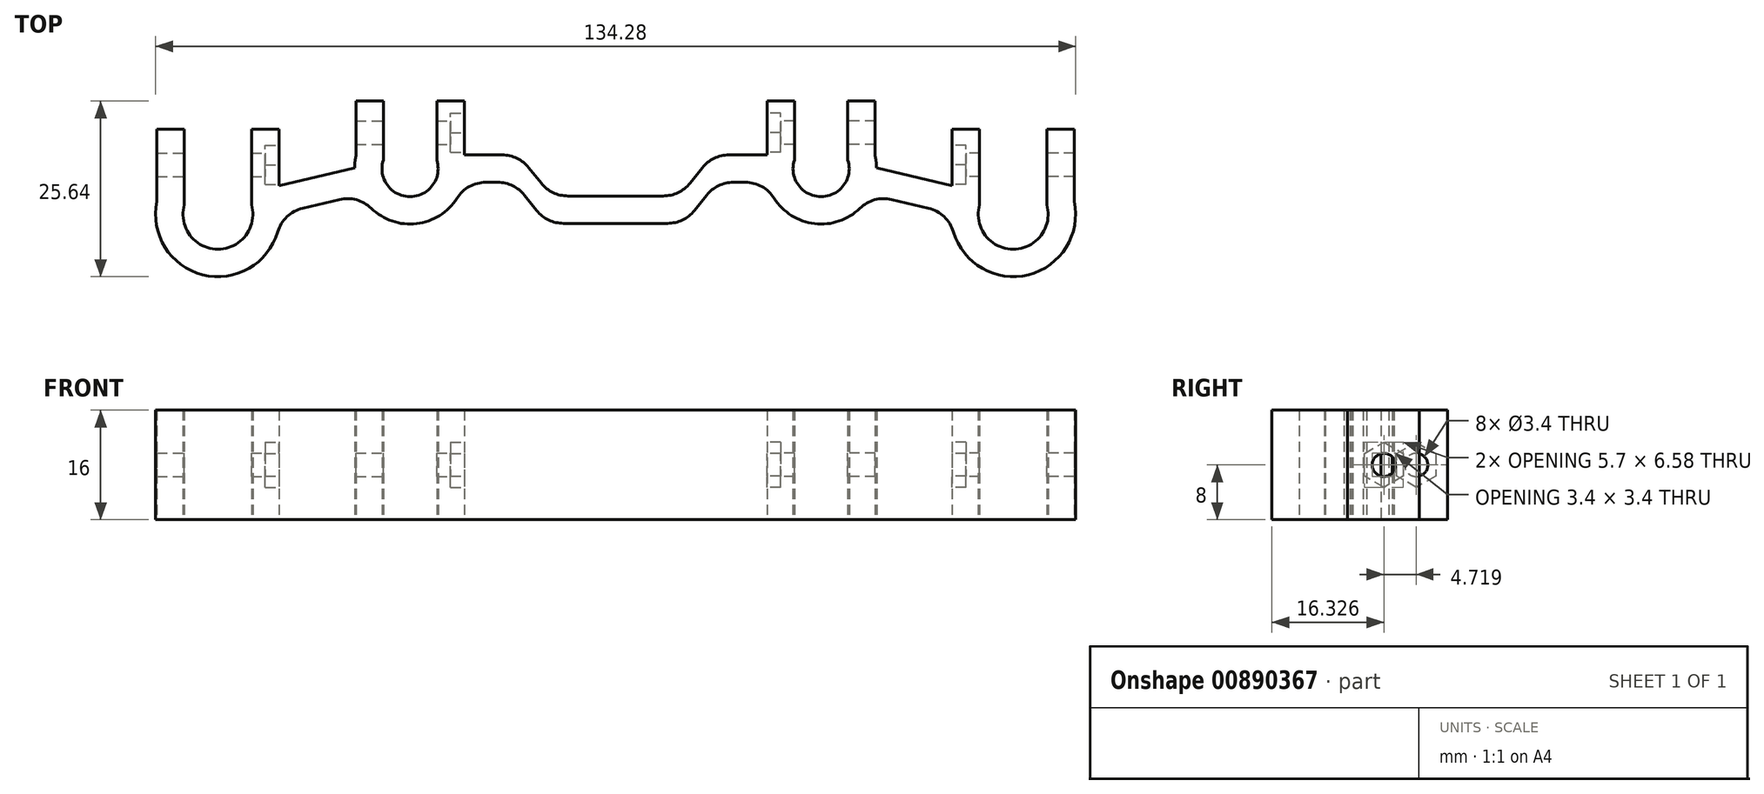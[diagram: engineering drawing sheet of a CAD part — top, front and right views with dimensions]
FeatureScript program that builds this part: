
annotation { "Feature Type Name" : "Feature", "Feature Type Description" : "" }
export const myFeature = defineFeature(function(context is Context, id is Id, definition is map)
    precondition{}
    {
        {
            var Q0;
            Q0=qCreatedBy(makeId("Top.planeOp"),FACE);
            var sketch = newSketch(context, id + "F0", { "sketchPlane" : qUnion([Q0])});
            skArc(sketch, "E0", {"start": v(-33.9, 1.26) * mm, "mid": v(-30, -4.1) * mm, "end": v(-26.1, 1.26) * mm});
            skArc(sketch, "E1", {"start": v(-62.94, -5.27) * mm, "mid": v(-58.04, -11.78) * mm, "end": v(-53.14, -5.27) * mm});
            skArc(sketch, "E2", {"start": v(-62.94, 0.99) * mm, "mid": v(-58.04, -15.78) * mm, "end": v(-53.14, 0.99) * mm});
            skArc(sketch, "E3", {"start": v(-33.9, 7.1) * mm, "mid": v(-30, -8.1) * mm, "end": v(-26.1, 7.1) * mm});
            skLineSegment(sketch, "E4", {"start": v(-58.04, -6.68) * mm, "end": v(-30, 0) * mm, "construction": true});
            skLineSegment(sketch, "E5", {"start": v(0, 0) * mm, "end": v(-30, 0) * mm, "construction": true});
            skLineSegment(sketch, "E6", {"start": v(-48.94, -6.57) * mm, "end": v(-37.17, -3.76) * mm});
            skLineSegment(sketch, "E7", {"start": v(-49.87, -2.68) * mm, "end": v(-38.1, 0.13) * mm});
            skLineSegment(sketch, "E8", {"start": v(-22.15, -2) * mm, "end": v(-16.15, -2) * mm});
            skLineSegment(sketch, "E9", {"start": v(-14.15, 2) * mm, "end": v(-22.15, 2) * mm});
            skLineSegment(sketch, "E10", {"start": v(-66.94, -4.78) * mm, "end": v(-66.94, 5.73) * mm});
            skLineSegment(sketch, "E11", {"start": v(-66.94, 5.73) * mm, "end": v(-62.94, 5.73) * mm});
            skLineSegment(sketch, "E12", {"start": v(-62.94, 5.73) * mm, "end": v(-62.94, -5.27) * mm});
            skLineSegment(sketch, "E13", {"start": v(-58.04, -5.27) * mm, "end": v(-66.94, -5.27) * mm, "construction": true});
            skLineSegment(sketch, "E14", {"start": v(-58.04, -6.68) * mm, "end": v(-58.04, 14.87) * mm, "construction": true});
            skLineSegment(sketch, "E15.MirrorCS", {"start": v(-53.14, 5.73) * mm, "end": v(-53.14, -5.27) * mm});
            skLineSegment(sketch, "E16.MirrorCS", {"start": v(-49.14, 5.73) * mm, "end": v(-53.14, 5.73) * mm});
            skLineSegment(sketch, "E17.MirrorCS", {"start": v(-49.14, -4.78) * mm, "end": v(-49.14, 5.73) * mm});
            skLineSegment(sketch, "E18", {"start": v(-30, 0) * mm, "end": v(-30, 14.05) * mm, "construction": true});
            skLineSegment(sketch, "E19", {"start": v(-37.9, 9.86) * mm, "end": v(-33.9, 9.86) * mm});
            skLineSegment(sketch, "E20", {"start": v(-33.9, 9.86) * mm, "end": v(-33.9, 1.26) * mm});
            skLineSegment(sketch, "E21.MirrorCS", {"start": v(-26.1, 9.86) * mm, "end": v(-26.1, 1.26) * mm});
            skLineSegment(sketch, "E22.MirrorCS", {"start": v(-22.1, 9.86) * mm, "end": v(-26.1, 9.86) * mm});
            skLineSegment(sketch, "E23", {"start": v(-37.9, 9.86) * mm, "end": v(-37.9, 1.79) * mm});
            skLineSegment(sketch, "E24.MirrorCS", {"start": v(-22.1, 9.86) * mm, "end": v(-22.1, 2) * mm});
            skPoint(sketch, "E25.orphan", {"position": v(-22.1, 1.79) * mm});
            skLineSegment(sketch, "E26", {"start": v(-14.15, 2) * mm, "end": v(-9.36, -4) * mm});
            skLineSegment(sketch, "E27", {"start": v(-9.36, -4) * mm, "end": v(-6, -4) * mm});
            skLineSegment(sketch, "E28", {"start": v(-14.8, -2) * mm, "end": v(-10, -8) * mm});
            skLineSegment(sketch, "E29", {"start": v(-10, -8) * mm, "end": v(0, -8) * mm});
            skLineSegment(sketch, "E30", {"start": v(0, -8) * mm, "end": v(0, -4) * mm});
            skLineSegment(sketch, "E31", {"start": v(-6, -4) * mm, "end": v(0, -4) * mm});
            skLineSegment(sketch, "E32", {"start": v(-16.15, -2) * mm, "end": v(-14.8, -2) * mm});
            skLineSegment(sketch, "E33", {"start": v(-9.36, -4) * mm, "end": v(-9.36, 12.5) * mm, "construction": true});
            skSolve(sketch);
        }
        {
            var Q0;
            Q0 = qSketchRegion(id + "F0", true);
            extrude(context, id + "F1", {"entities" : qUnion([Q0]), "depth" : 16 * mm, "offsetDistance" : 25 * mm});
        }
        {
            var Q0;
            Q0=makeQuery(id+"F1.opExtrude","SWEPT_FACE",FACE,{"disambiguationData":[OSD([sQuery(id+"F0.wireOp",EDGE,"E24.MirrorCS")])]});
            var sketch = newSketch(context, id + "F2", { "sketchPlane" : qUnion([Q0])});
            skCircle(sketch, "E34.cCircle", {"center": v(5.26, 8) * mm, "radius": 2.85 * mm, "construction": true});
            skLineSegment(sketch, "E34.0", {"start": v(8.11, 9.65) * mm, "end": v(8.11, 6.35) * mm});
            skLineSegment(sketch, "E34.1", {"start": v(8.11, 6.35) * mm, "end": v(5.26, 4.7) * mm});
            skLineSegment(sketch, "E34.2", {"start": v(5.26, 4.7) * mm, "end": v(2.41, 6.35) * mm});
            skLineSegment(sketch, "E34.3", {"start": v(2.41, 6.35) * mm, "end": v(2.41, 9.65) * mm});
            skLineSegment(sketch, "E34.4", {"start": v(2.41, 9.65) * mm, "end": v(5.26, 11.3) * mm});
            skLineSegment(sketch, "E34.5", {"start": v(5.26, 11.3) * mm, "end": v(8.11, 9.65) * mm});
            skPoint(sketch, "E34.0.midPoint", {"position": v(8.11, 8) * mm});
            skLineSegment(sketch, "E35", {"start": v(9.86, 8) * mm, "end": v(-7.7, 8) * mm, "construction": true});
            skCircle(sketch, "E36", {"center": v(5.26, 8) * mm, "radius": 1.7 * mm});
            skSolve(sketch);
        }
        {
            var Q0;
            Q0=makeQuery(id+"F2.imprint","IMPRINT",FACE,{"disambiguationData":[TD([[makeQuery(id+"F2.imprint","IMPRINT",EDGE,{"derivedFrom":sQuery(id+"F2.wireOp",EDGE,"b88b7a63-ffb0-4f3f-a911-7858551cdc820.MirrorC")}),-1.0]])]});
            var Q1;
            Q1=makeQuery(id+"F2.imprint","IMPRINT",FACE,{"disambiguationData":[TD([[makeQuery(id+"F2.imprint","IMPRINT",EDGE,{"derivedFrom":sQuery(id+"F2.wireOp",EDGE,"E36")}),1.0]])]});
            var Q2;
            Q2=makeQuery(id+"F1.opExtrude","SWEPT_FACE",FACE,{"disambiguationData":[OSD([sQuery(id+"F0.wireOp",EDGE,"E23")])]});
            extrude(context, id + "F3", {"entities" : qUnion([Q0, Q1]), "operationType" : NewBodyOperationType.REMOVE, "endBound" : BoundingType.UP_TO_SURFACE, "oppositeDirection" : true, "depth" : 25 * mm, "endBoundEntityFace" : qUnion([Q2]), "offsetDistance" : 25 * mm});
        }
        {
            var Q0;
            Q0=makeQuery(id+"F2.imprint","IMPRINT",FACE,{"disambiguationData":[TD([[makeQuery(id+"F2.imprint","IMPRINT",EDGE,{"derivedFrom":sQuery(id+"F2.wireOp",EDGE,"1b03209d-ab96-45ee-9a79-0f29908199c00.MirrorCS")}),1.0]])]});
            var Q1;
            Q1=makeQuery(id+"F2.imprint","IMPRINT",FACE,{"disambiguationData":[TD([[makeQuery(id+"F2.imprint","IMPRINT",EDGE,{"derivedFrom":sQuery(id+"F2.wireOp",EDGE,"E34.0")}),-1.0]])]});
            extrude(context, id + "F4", {"entities" : qUnion([Q0, Q1]), "operationType" : NewBodyOperationType.REMOVE, "oppositeDirection" : true, "depth" : 2 * mm, "offsetDistance" : 25 * mm});
        }
        {
            var Q0;
            Q0=makeQuery(id+"F1.opExtrude","SWEPT_FACE",FACE,{"disambiguationData":[OSD([sQuery(id+"F0.wireOp",EDGE,"E17.MirrorCS")])]});
            var sketch = newSketch(context, id + "F5", { "sketchPlane" : qUnion([Q0])});
            skCircle(sketch, "E37.cCircle", {"center": v(0.55, 8) * mm, "radius": 2.85 * mm, "construction": true});
            skLineSegment(sketch, "E37.0", {"start": v(3.4, 9.65) * mm, "end": v(3.4, 6.35) * mm});
            skLineSegment(sketch, "E37.1", {"start": v(3.4, 6.35) * mm, "end": v(0.55, 4.7) * mm});
            skLineSegment(sketch, "E37.2", {"start": v(0.55, 4.7) * mm, "end": v(-2.3, 6.35) * mm});
            skLineSegment(sketch, "E37.3", {"start": v(-2.3, 6.35) * mm, "end": v(-2.3, 9.65) * mm});
            skLineSegment(sketch, "E37.4", {"start": v(-2.3, 9.65) * mm, "end": v(0.55, 11.3) * mm});
            skLineSegment(sketch, "E37.5", {"start": v(0.55, 11.3) * mm, "end": v(3.4, 9.65) * mm});
            skPoint(sketch, "E37.0.midPoint", {"position": v(3.4, 8) * mm});
            skLineSegment(sketch, "E38", {"start": v(5.73, 8) * mm, "end": v(4.73, 8) * mm, "construction": true});
            skPoint(sketch, "E38.startSnap0", {"position": v(5.73, 8) * mm});
            skCircle(sketch, "E39", {"center": v(0.55, 8) * mm, "radius": 1.7 * mm});
            skSolve(sketch);
        }
        {
            var Q0;
            Q0=makeQuery(id+"F5.imprint","IMPRINT",FACE,{"disambiguationData":[TD([[makeQuery(id+"F5.imprint","IMPRINT",EDGE,{"derivedFrom":sQuery(id+"F5.wireOp",EDGE,"b51dffc8-de77-4591-ae2f-6b328c8c791c0.MirrorC")}),-1.0]])]});
            var Q1;
            Q1=makeQuery(id+"F5.imprint","IMPRINT",FACE,{"disambiguationData":[TD([[makeQuery(id+"F5.imprint","IMPRINT",EDGE,{"derivedFrom":sQuery(id+"F5.wireOp",EDGE,"E39")}),1.0]])]});
            var Q2;
            Q2=makeQuery(id+"F1.opExtrude","SWEPT_FACE",FACE,{"disambiguationData":[OSD([sQuery(id+"F0.wireOp",EDGE,"E10")])]});
            extrude(context, id + "F6", {"entities" : qUnion([Q0, Q1]), "operationType" : NewBodyOperationType.REMOVE, "endBound" : BoundingType.UP_TO_SURFACE, "oppositeDirection" : true, "depth" : 25 * mm, "endBoundEntityFace" : qUnion([Q2]), "offsetDistance" : 25 * mm});
        }
        {
            var Q0;
            Q0=makeQuery(id+"F5.imprint","IMPRINT",FACE,{"disambiguationData":[TD([[makeQuery(id+"F5.imprint","IMPRINT",EDGE,{"derivedFrom":sQuery(id+"F5.wireOp",EDGE,"E37.0")}),-1.0]])]});
            var Q1;
            {var subQ1=sQuery(id+"F5.wireOp",EDGE,"86751706-22c6-47e1-9a94-7943053e6f4f0.MirrorCS");Q1=makeQuery(id+"F5.imprint","IMPRINT",FACE,{"disambiguationData":[TD([[makeQuery(id+"F5.imprint","IMPRINT",EDGE,{"derivedFrom":subQ1}),1.0]])]});}
            extrude(context, id + "F7", {"entities" : qUnion([Q0, Q1]), "operationType" : NewBodyOperationType.REMOVE, "oppositeDirection" : true, "depth" : 2 * mm, "offsetDistance" : 25 * mm});
        }
        {
            var Q0;
            Q0=makeQuery(id+"F1.opExtrude","SWEPT_EDGE",EDGE,{"disambiguationData":[OSD([sQuery(id+"F0.wireOp",EDGE,"E2"),sQuery(id+"F0.wireOp",EDGE,"E6")])]});
            var Q1;
            Q1=makeQuery(id+"F1.opExtrude","SWEPT_EDGE",EDGE,{"disambiguationData":[OSD([sQuery(id+"F0.wireOp",EDGE,"E3"),sQuery(id+"F0.wireOp",EDGE,"E6")])]});
            var Q2;
            Q2=makeQuery(id+"F1.opExtrude","SWEPT_EDGE",EDGE,{"disambiguationData":[OSD([sQuery(id+"F0.wireOp",EDGE,"E3"),sQuery(id+"F0.wireOp",EDGE,"E8")])]});
            var Q3;
            Q3=makeQuery(id+"F1.opExtrude","SWEPT_EDGE",EDGE,{"disambiguationData":[OSD([sQuery(id+"F0.wireOp",EDGE,"E28"),sQuery(id+"F0.wireOp",EDGE,"E32")])]});
            var Q4;
            Q4=makeQuery(id+"F1.opExtrude","SWEPT_EDGE",EDGE,{"disambiguationData":[OSD([sQuery(id+"F0.wireOp",EDGE,"E28"),sQuery(id+"F0.wireOp",EDGE,"E29")])]});
            var Q5;
            Q5=makeQuery(id+"F1.opExtrude","SWEPT_EDGE",EDGE,{"disambiguationData":[OSD([sQuery(id+"F0.wireOp",EDGE,"E26"),sQuery(id+"F0.wireOp",EDGE,"E27")])]});
            var Q6;
            Q6=makeQuery(id+"F1.opExtrude","SWEPT_EDGE",EDGE,{"disambiguationData":[OSD([sQuery(id+"F0.wireOp",EDGE,"E9"),sQuery(id+"F0.wireOp",EDGE,"E26")])]});
            fillet(context, id + "F8", {"entities" : qUnion([Q0, Q1, Q2, Q3, Q4, Q5, Q6]), "radius" : 5 * mm, "tangentPropagation" : true, "allowEdgeOverflow" : false});
        }
        {
            var Q0;
            Q0=makeQuery(id+"F1.opExtrude","SWEPT_BODY",BODY,{"disambiguationData":[OSD([sQuery(id+"F0.wireOp",EDGE,"E0"),sQuery(id+"F0.wireOp",EDGE,"E1"),sQuery(id+"F0.wireOp",EDGE,"E2"),sQuery(id+"F0.wireOp",EDGE,"E3"),sQuery(id+"F0.wireOp",EDGE,"E6"),sQuery(id+"F0.wireOp",EDGE,"E7"),sQuery(id+"F0.wireOp",EDGE,"E8"),sQuery(id+"F0.wireOp",EDGE,"l0BjIGxy-IBX7-E7l8-Vuus-eviOhHEXfN3c"),sQuery(id+"F0.wireOp",EDGE,"E9"),sQuery(id+"F0.wireOp",EDGE,"E11"),sQuery(id+"F0.wireOp",EDGE,"E12"),sQuery(id+"F0.wireOp",EDGE,"E15.MirrorCS"),sQuery(id+"F0.wireOp",EDGE,"E16.MirrorCS"),sQuery(id+"F0.wireOp",EDGE,"E17.MirrorCS"),sQuery(id+"F0.wireOp",EDGE,"E10"),sQuery(id+"F0.wireOp",EDGE,"pgNTpAga-basL-g0mY-hS2O-fjBzi6c6udV9"),sQuery(id+"F0.wireOp",EDGE,"E19"),sQuery(id+"F0.wireOp",EDGE,"E20"),sQuery(id+"F0.wireOp",EDGE,"E21.MirrorCS"),sQuery(id+"F0.wireOp",EDGE,"E22.MirrorCS"),sQuery(id+"F0.wireOp",EDGE,"77d6a375-33a9-4cfe-885e-65678774e27b0.MirrorCS")])]});
            var Q1;
            Q1=qCreatedBy(makeId("Right.planeOp"),FACE);
            mirror(context, id + "F9", {"operationType" : NewBodyOperationType.ADD, "entities" : qUnion([Q0]), "mirrorPlane" : qUnion([Q1])});
        }
    });
